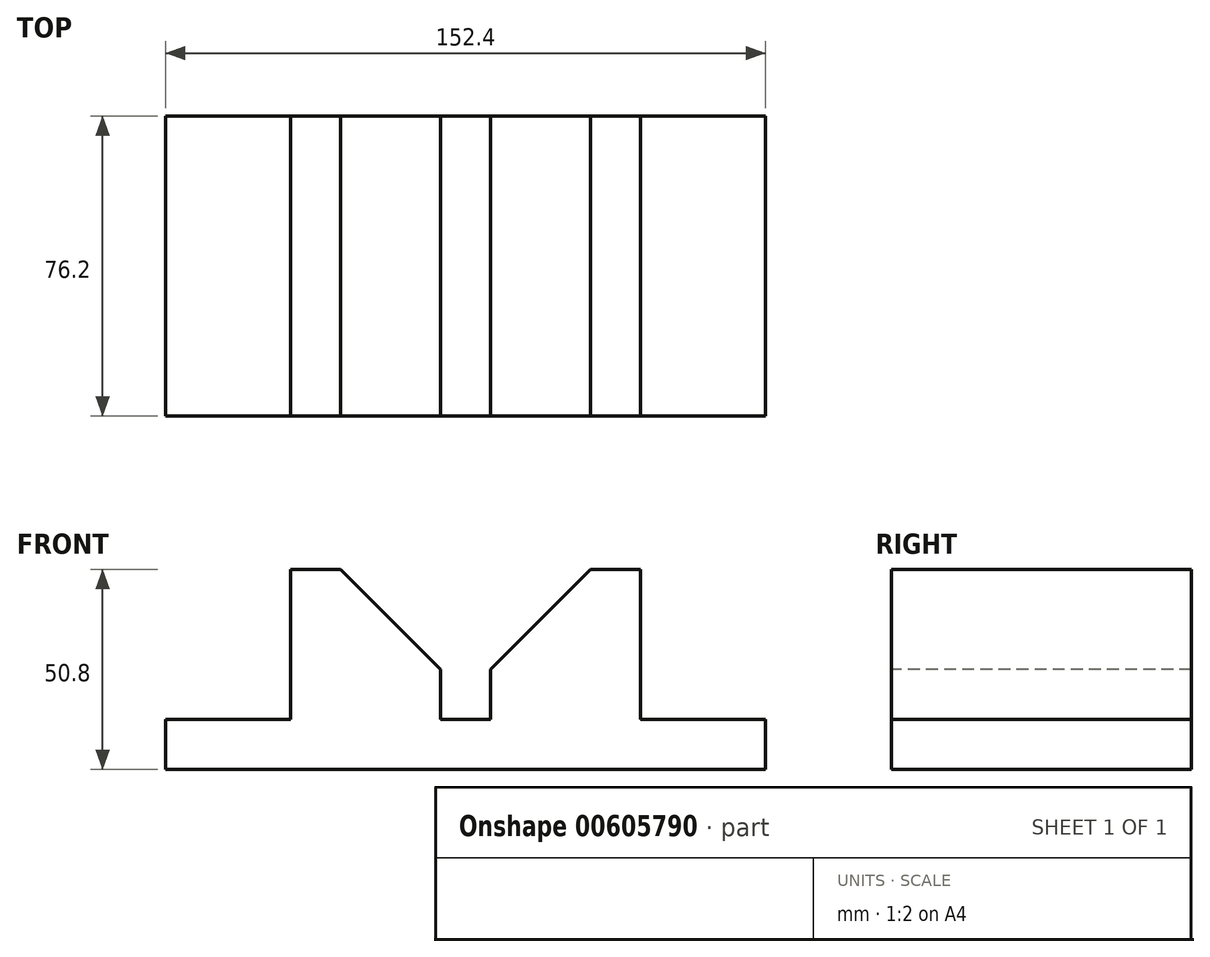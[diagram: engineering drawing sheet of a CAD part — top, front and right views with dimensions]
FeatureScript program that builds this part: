
annotation { "Feature Type Name" : "Feature", "Feature Type Description" : "" }
export const myFeature = defineFeature(function(context is Context, id is Id, definition is map)
    precondition{}
    {
        {
            var Q0;
            Q0=qCreatedBy(makeId("Front.planeOp"),FACE);
            var sketch = newSketch(context, id + "F0", { "sketchPlane" : qUnion([Q0])});
            skLineSegment(sketch, "E0", {"start": v(0, 0) * mm, "end": v(152.4, 0) * mm});
            skLineSegment(sketch, "E1", {"start": v(152.4, 50.8) * mm, "end": v(152.4, 0) * mm});
            skLineSegment(sketch, "E2", {"start": v(0, 50.8) * mm, "end": v(0, 0) * mm});
            skLineSegment(sketch, "E3", {"start": v(0, 50.8) * mm, "end": v(152.4, 50.8) * mm});
            skSolve(sketch);
        }
        {
            var Q0;
            Q0 = qSketchRegion(id + "F0", true);
            extrude(context, id + "F1", {"entities" : qUnion([Q0]), "depth" : 76.2 * mm, "offsetDistance" : 25.4 * mm});
        }
        {
            var Q0;
            Q0=makeQuery(id+"F1.opExtrude","CAP_FACE",FACE,{"disambiguationData":[OSD([sQuery(id+"F0.wireOp",EDGE,"E0"),sQuery(id+"F0.wireOp",EDGE,"E1"),sQuery(id+"F0.wireOp",EDGE,"E2"),sQuery(id+"F0.wireOp",EDGE,"E3")])],"isStart":false});
            var sketch = newSketch(context, id + "F2", { "sketchPlane" : qUnion([Q0])});
            skLineSegment(sketch, "E4", {"start": v(0, 0) * mm, "end": v(0, 12.7) * mm});
            skLineSegment(sketch, "E5", {"start": v(152.4, 0) * mm, "end": v(152.4, 12.7) * mm});
            skLineSegment(sketch, "E6", {"start": v(152.4, 12.7) * mm, "end": v(120.65, 12.7) * mm});
            skLineSegment(sketch, "E7", {"start": v(0, 12.7) * mm, "end": v(31.75, 12.7) * mm});
            skLineSegment(sketch, "E8", {"start": v(31.75, 12.7) * mm, "end": v(31.75, 50.8) * mm});
            skLineSegment(sketch, "E9", {"start": v(31.75, 50.8) * mm, "end": v(0, 50.8) * mm});
            skLineSegment(sketch, "E10", {"start": v(0, 50.8) * mm, "end": v(0, 12.7) * mm});
            skSolve(sketch);
        }
        {
            var Q0;
            Q0 = qSketchRegion(id + "F2", true);
            extrude(context, id + "F3", {"entities" : qUnion([Q0]), "operationType" : NewBodyOperationType.ADD, "depth" : 25.4 * mm, "offsetDistance" : 25.4 * mm});
        }
        {
            var Q0;
            Q0=makeQuery(id+"F3.opExtrude","CAP_FACE",FACE,{"disambiguationData":[OSD([sQuery(id+"F2.wireOp",EDGE,"E7"),sQuery(id+"F2.wireOp",EDGE,"E8"),sQuery(id+"F2.wireOp",EDGE,"E9"),sQuery(id+"F2.wireOp",EDGE,"E10")])],"isStart":false});
            extrude(context, id + "F4", {"entities" : qUnion([Q0]), "operationType" : NewBodyOperationType.REMOVE, "oppositeDirection" : true, "depth" : 101.6 * mm, "offsetDistance" : 25.4 * mm});
        }
        {
            var Q0;
            Q0=makeQuery(id+"F1.opExtrude","CAP_FACE",FACE,{"disambiguationData":[OSD([sQuery(id+"F0.wireOp",EDGE,"E0"),sQuery(id+"F0.wireOp",EDGE,"E1"),sQuery(id+"F0.wireOp",EDGE,"E2"),sQuery(id+"F0.wireOp",EDGE,"E3")])],"isStart":false});
            var sketch = newSketch(context, id + "F5", { "sketchPlane" : qUnion([Q0])});
            skLineSegment(sketch, "E11", {"start": v(152.4, 0) * mm, "end": v(152.4, 12.7) * mm});
            skLineSegment(sketch, "E12", {"start": v(152.4, 12.7) * mm, "end": v(120.65, 12.7) * mm});
            skLineSegment(sketch, "E13", {"start": v(120.65, 12.7) * mm, "end": v(120.65, 50.8) * mm});
            skLineSegment(sketch, "E14", {"start": v(120.65, 50.8) * mm, "end": v(152.4, 50.8) * mm});
            skLineSegment(sketch, "E15", {"start": v(152.4, 50.8) * mm, "end": v(152.4, 12.7) * mm});
            skSolve(sketch);
        }
        {
            var Q0;
            Q0 = qSketchRegion(id + "F5", true);
            extrude(context, id + "F6", {"entities" : qUnion([Q0]), "operationType" : NewBodyOperationType.REMOVE, "oppositeDirection" : true, "depth" : 76.2 * mm, "offsetDistance" : 25.4 * mm});
        }
        {
            var Q0;
            Q0=makeQuery(id+"F1.opExtrude","CAP_FACE",FACE,{"disambiguationData":[OSD([sQuery(id+"F0.wireOp",EDGE,"E0"),sQuery(id+"F0.wireOp",EDGE,"E1"),sQuery(id+"F0.wireOp",EDGE,"E2"),sQuery(id+"F0.wireOp",EDGE,"E3")])],"isStart":false});
            var sketch = newSketch(context, id + "F7", { "sketchPlane" : qUnion([Q0])});
            skLineSegment(sketch, "E16", {"start": v(31.75, 50.8) * mm, "end": v(69.85, 50.8) * mm});
            skLineSegment(sketch, "E17", {"start": v(120.65, 50.8) * mm, "end": v(82.55, 50.8) * mm});
            skLineSegment(sketch, "E18", {"start": v(69.85, 50.8) * mm, "end": v(69.85, 25.4) * mm});
            skLineSegment(sketch, "E19", {"start": v(82.55, 50.8) * mm, "end": v(82.55, 25.4) * mm});
            skLineSegment(sketch, "E20", {"start": v(31.75, 50.8) * mm, "end": v(44.45, 50.8) * mm});
            skLineSegment(sketch, "E21", {"start": v(120.65, 50.8) * mm, "end": v(107.95, 50.8) * mm});
            skLineSegment(sketch, "E22", {"start": v(44.45, 50.8) * mm, "end": v(69.85, 25.4) * mm});
            skLineSegment(sketch, "E23", {"start": v(69.85, 50.8) * mm, "end": v(44.45, 50.8) * mm});
            skLineSegment(sketch, "E24", {"start": v(107.95, 50.8) * mm, "end": v(82.55, 25.4) * mm});
            skLineSegment(sketch, "E25", {"start": v(82.55, 50.8) * mm, "end": v(107.95, 50.8) * mm});
            skSolve(sketch);
        }
        {
            var Q0;
            Q0 = qSketchRegion(id + "F7", true);
            extrude(context, id + "F8", {"entities" : qUnion([Q0]), "operationType" : NewBodyOperationType.REMOVE, "oppositeDirection" : true, "depth" : 76.2 * mm, "offsetDistance" : 25.4 * mm});
        }
        {
            var Q0;
            Q0=makeQuery(id+"F1.opExtrude","CAP_FACE",FACE,{"disambiguationData":[OSD([sQuery(id+"F0.wireOp",EDGE,"E0"),sQuery(id+"F0.wireOp",EDGE,"E1"),sQuery(id+"F0.wireOp",EDGE,"E2"),sQuery(id+"F0.wireOp",EDGE,"E3")])],"isStart":false});
            var sketch = newSketch(context, id + "F9", { "sketchPlane" : qUnion([Q0])});
            skLineSegment(sketch, "E26", {"start": v(69.85, 25.4) * mm, "end": v(82.55, 25.4) * mm});
            skLineSegment(sketch, "E27", {"start": v(82.55, 25.4) * mm, "end": v(82.55, 50.8) * mm});
            skLineSegment(sketch, "E28", {"start": v(82.55, 50.8) * mm, "end": v(69.85, 50.8) * mm});
            skLineSegment(sketch, "E29", {"start": v(69.85, 50.8) * mm, "end": v(69.85, 25.4) * mm});
            skSolve(sketch);
        }
        {
            var Q0;
            Q0 = qSketchRegion(id + "F9", true);
            extrude(context, id + "F10", {"entities" : qUnion([Q0]), "operationType" : NewBodyOperationType.REMOVE, "oppositeDirection" : true, "depth" : 76.2 * mm, "offsetDistance" : 25.4 * mm});
        }
        {
            var Q0;
            Q0=makeQuery(id+"F1.opExtrude","CAP_FACE",FACE,{"disambiguationData":[OSD([sQuery(id+"F0.wireOp",EDGE,"E0"),sQuery(id+"F0.wireOp",EDGE,"E1"),sQuery(id+"F0.wireOp",EDGE,"E2"),sQuery(id+"F0.wireOp",EDGE,"E3")])],"isStart":false});
            var sketch = newSketch(context, id + "F11", { "sketchPlane" : qUnion([Q0])});
            skLineSegment(sketch, "E30", {"start": v(69.85, 25.4) * mm, "end": v(69.85, 12.7) * mm});
            skLineSegment(sketch, "E31", {"start": v(69.85, 12.7) * mm, "end": v(82.55, 12.7) * mm});
            skLineSegment(sketch, "E32", {"start": v(82.55, 12.7) * mm, "end": v(82.55, 25.4) * mm});
            skSolve(sketch);
        }
        {
            var Q0;
            Q0 = qSketchRegion(id + "F11", true);
            var Q1;
            Q1=makeQuery(id+"F11.imprint","IMPRINT",FACE,{"disambiguationData":[TD([[makeQuery(id+"F11.imprint","IMPRINT",EDGE,{"derivedFrom":sQuery(id+"F11.wireOp",EDGE,"E30")}),1.0]])]});
            extrude(context, id + "F12", {"entities" : qUnion([Q0, Q1]), "operationType" : NewBodyOperationType.REMOVE, "oppositeDirection" : true, "depth" : 76.2 * mm, "offsetDistance" : 25.4 * mm});
        }
    });
